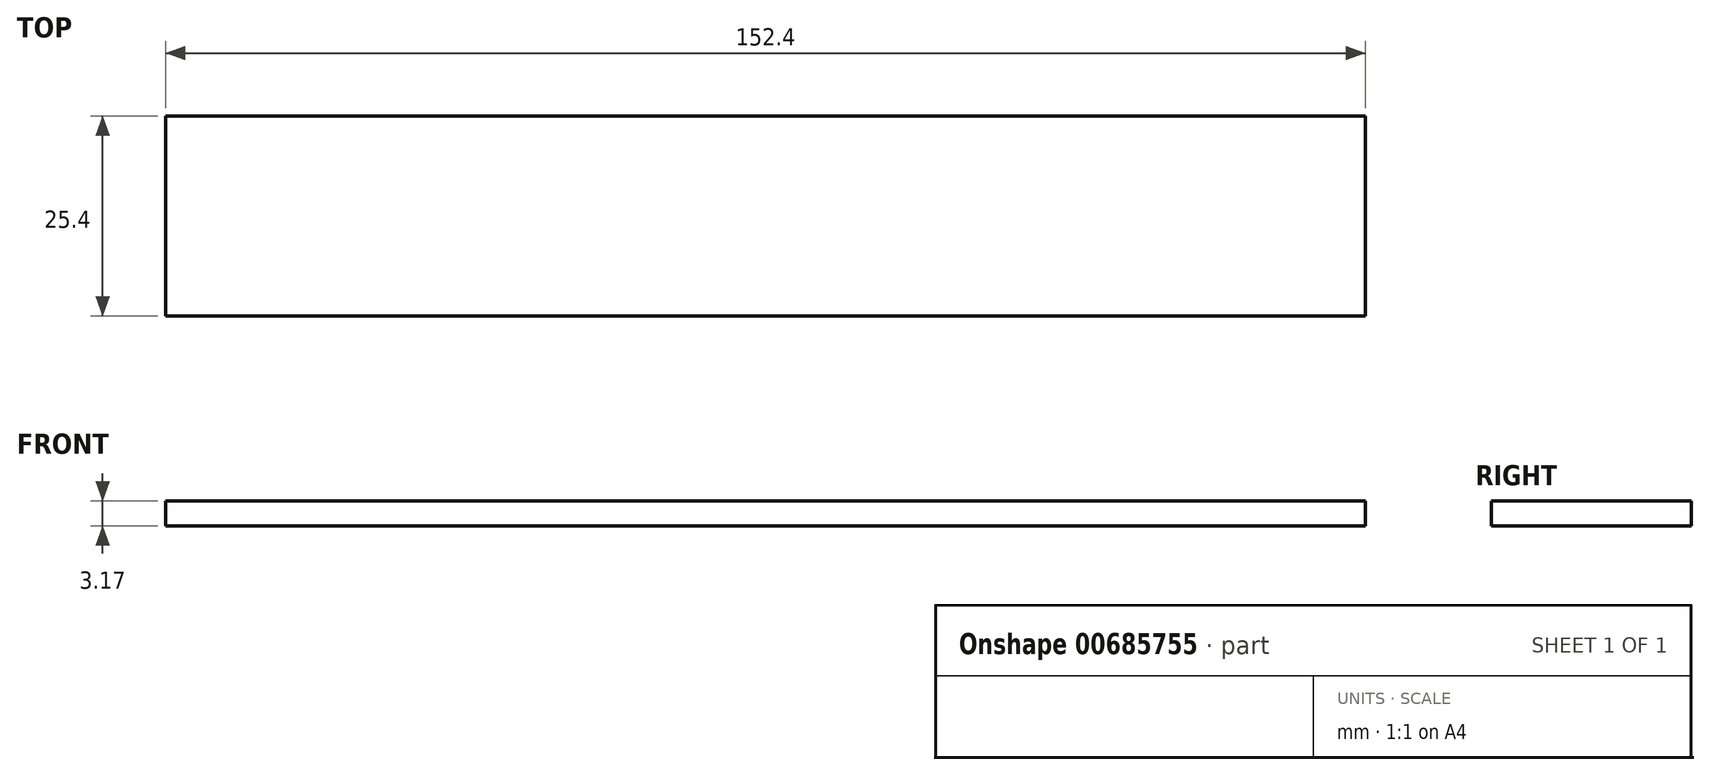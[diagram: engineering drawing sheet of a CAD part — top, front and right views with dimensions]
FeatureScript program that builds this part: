
annotation { "Feature Type Name" : "Feature", "Feature Type Description" : "" }
export const myFeature = defineFeature(function(context is Context, id is Id, definition is map)
    precondition{}
    {
        {
            var Q0;
            Q0=qCreatedBy(makeId("Top.planeOp"),FACE);
            var sketch = newSketch(context, id + "F0", { "sketchPlane" : qUnion([Q0])});
            skLineSegment(sketch, "E0.bottom", {"start": v(0, 0) * mm, "end": v(152.4, 0) * mm});
            skLineSegment(sketch, "E0.top", {"start": v(0, 25.4) * mm, "end": v(152.4, 25.4) * mm});
            skLineSegment(sketch, "E0.left", {"start": v(0, 0) * mm, "end": v(0, 25.4) * mm});
            skLineSegment(sketch, "E0.right", {"start": v(152.4, 0) * mm, "end": v(152.4, 25.4) * mm});
            skPoint(sketch, "E1", {"position": v(139.7, 12.7) * mm});
            skPoint(sketch, "E2", {"position": v(12.7, 12.7) * mm});
            skCircle(sketch, "E3", {"center": v(12.7, 12.7) * mm, "radius": 3.18 * mm});
            skCircle(sketch, "E4", {"center": v(139.7, 12.7) * mm, "radius": 3.18 * mm});
            skSolve(sketch);
        }
        {
            var Q0;
            Q0=makeQuery(id+"F0.imprint","IMPRINT",FACE,{"disambiguationData":[TD([[makeQuery(id+"F0.imprint","IMPRINT",EDGE,{"derivedFrom":sQuery(id+"F0.wireOp",EDGE,"E0.bottom")}),1.0]])]});
            var Q1;
            Q1=makeQuery(id+"F0.imprint","IMPRINT",FACE,{"disambiguationData":[TD([[makeQuery(id+"F0.imprint","IMPRINT",EDGE,{"derivedFrom":sQuery(id+"F0.wireOp",EDGE,"E3")}),1.0]])]});
            var Q2;
            Q2=makeQuery(id+"F0.imprint","IMPRINT",FACE,{"disambiguationData":[TD([[makeQuery(id+"F0.imprint","IMPRINT",EDGE,{"derivedFrom":sQuery(id+"F0.wireOp",EDGE,"E4")}),1.0]])]});
            extrude(context, id + "F1", {"entities" : qUnion([Q0, Q1, Q2]), "depth" : 3.17 * mm});
        }
    });
